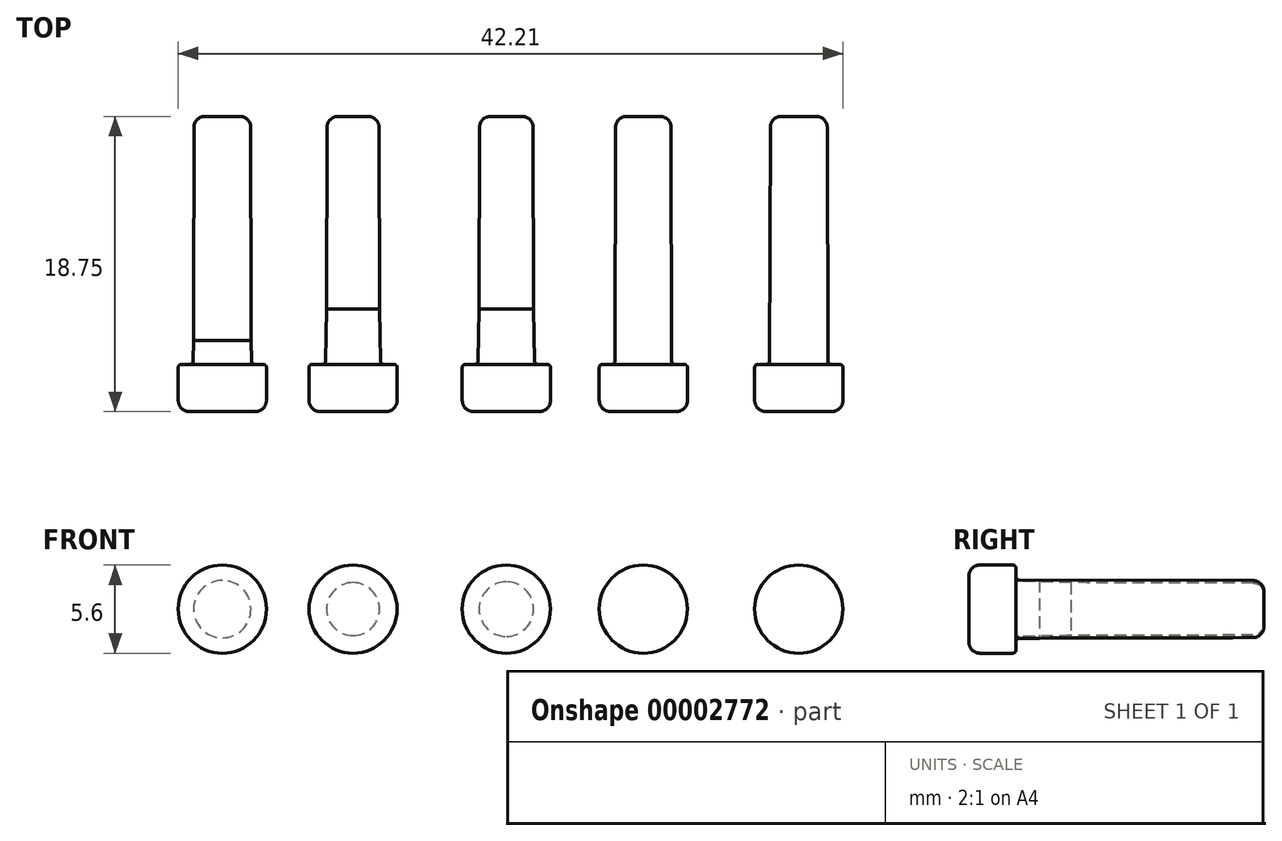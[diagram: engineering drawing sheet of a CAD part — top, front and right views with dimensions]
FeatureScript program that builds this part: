
annotation { "Feature Type Name" : "Feature", "Feature Type Description" : "" }
export const myFeature = defineFeature(function(context is Context, id is Id, definition is map)
    precondition{}
    {
        {
            var Q0;
            Q0=qCreatedBy(makeId("Top.planeOp"),FACE);
            var sketch = newSketch(context, id + "F0", { "sketchPlane" : qUnion([Q0])});
            skLineSegment(sketch, "E0", {"start": v(0, 0) * mm, "end": v(-2.8, 0) * mm});
            skLineSegment(sketch, "E1", {"start": v(-2.8, 0) * mm, "end": v(-2.8, 3) * mm});
            skLineSegment(sketch, "E2", {"start": v(-2.8, 3) * mm, "end": v(-1.8, 3) * mm});
            skLineSegment(sketch, "E3", {"start": v(-1.7, 18.75) * mm, "end": v(0, 18.75) * mm});
            skLineSegment(sketch, "E4", {"start": v(0, 18.75) * mm, "end": v(0, 0) * mm});
            skLineSegment(sketch, "E5", {"start": v(-9.74, 0) * mm, "end": v(-12.54, 0) * mm});
            skLineSegment(sketch, "E6", {"start": v(-12.54, 0) * mm, "end": v(-12.54, 3) * mm});
            skLineSegment(sketch, "E7", {"start": v(-12.54, 3) * mm, "end": v(-11.49, 3) * mm});
            skLineSegment(sketch, "E8", {"start": v(-11.39, 18.75) * mm, "end": v(-9.74, 18.75) * mm});
            skLineSegment(sketch, "E9", {"start": v(-9.74, 18.75) * mm, "end": v(-9.74, 0) * mm});
            skLineSegment(sketch, "E10", {"start": v(8.7, 0) * mm, "end": v(5.9, 0) * mm});
            skLineSegment(sketch, "E11", {"start": v(5.9, 0) * mm, "end": v(5.9, 3) * mm});
            skLineSegment(sketch, "E12", {"start": v(5.9, 3) * mm, "end": v(6.9, 3) * mm});
            skLineSegment(sketch, "E13", {"start": v(6.9, 3) * mm, "end": v(6.94, 18.75) * mm});
            skLineSegment(sketch, "E14", {"start": v(6.94, 18.75) * mm, "end": v(8.7, 18.75) * mm});
            skLineSegment(sketch, "E15", {"start": v(8.7, 18.75) * mm, "end": v(8.7, 0) * mm});
            skLineSegment(sketch, "E16", {"start": v(18.57, 0) * mm, "end": v(15.77, 0) * mm});
            skLineSegment(sketch, "E17", {"start": v(15.77, 0) * mm, "end": v(15.77, 3) * mm});
            skLineSegment(sketch, "E18", {"start": v(15.77, 3) * mm, "end": v(16.72, 3) * mm});
            skLineSegment(sketch, "E19", {"start": v(16.72, 3) * mm, "end": v(16.76, 18.75) * mm});
            skLineSegment(sketch, "E20", {"start": v(16.76, 18.75) * mm, "end": v(18.57, 18.75) * mm});
            skLineSegment(sketch, "E21", {"start": v(18.57, 18.75) * mm, "end": v(18.57, 0) * mm});
            skLineSegment(sketch, "E22", {"start": v(-18.04, 0) * mm, "end": v(-20.84, 0) * mm});
            skLineSegment(sketch, "E23", {"start": v(-20.84, 0) * mm, "end": v(-20.84, 3) * mm});
            skLineSegment(sketch, "E24", {"start": v(-20.84, 3) * mm, "end": v(-19.89, 3) * mm});
            skLineSegment(sketch, "E25", {"start": v(-19.84, 18.75) * mm, "end": v(-18.04, 18.75) * mm});
            skLineSegment(sketch, "E26", {"start": v(-18.04, 18.75) * mm, "end": v(-18.04, 0) * mm});
            skLineSegment(sketch, "E27", {"start": v(-1.8, 3) * mm, "end": v(-1.77, 4.5) * mm});
            skLineSegment(sketch, "E28", {"start": v(-1.77, 4.5) * mm, "end": v(-1.73, 6.5) * mm});
            skLineSegment(sketch, "E29", {"start": v(-1.73, 6.5) * mm, "end": v(-1.7, 18.75) * mm});
            skLineSegment(sketch, "E30", {"start": v(-11.49, 3) * mm, "end": v(-11.46, 4.5) * mm});
            skLineSegment(sketch, "E31", {"start": v(-11.46, 4.5) * mm, "end": v(-11.42, 6.5) * mm});
            skLineSegment(sketch, "E32", {"start": v(-11.42, 6.5) * mm, "end": v(-11.39, 18.75) * mm});
            skLineSegment(sketch, "E33", {"start": v(-19.89, 3) * mm, "end": v(-19.86, 4.5) * mm});
            skLineSegment(sketch, "E34", {"start": v(-19.86, 4.5) * mm, "end": v(-19.87, 6.5) * mm});
            skLineSegment(sketch, "E35", {"start": v(-19.87, 6.5) * mm, "end": v(-19.84, 18.75) * mm});
            skSolve(sketch);
        }
        {
            var Q0;
            Q0=makeQuery(id+"F0.imprint","IMPRINT",FACE,{"disambiguationData":[TD([[makeQuery(id+"F0.imprint","IMPRINT",EDGE,{"derivedFrom":sQuery(id+"F0.wireOp",EDGE,"E22")}),-1.0]])]});
            var Q1;
            Q1=sQuery(id+"F0.wireOp",EDGE,"E26");
            revolve(context, id + "F1", {"entities" : qUnion([Q0]), "axis" : qUnion([Q1]), "revolveType" : RevolveType.FULL});
        }
        {
            var Q0;
            Q0=makeQuery(id+"F0.imprint","IMPRINT",FACE,{"disambiguationData":[TD([[makeQuery(id+"F0.imprint","IMPRINT",EDGE,{"derivedFrom":sQuery(id+"F0.wireOp",EDGE,"E5")}),-1.0]])]});
            var Q1;
            Q1=sQuery(id+"F0.wireOp",EDGE,"E9");
            revolve(context, id + "F2", {"entities" : qUnion([Q0]), "axis" : qUnion([Q1]), "revolveType" : RevolveType.FULL});
        }
        {
            var Q0;
            Q0=makeQuery(id+"F0.imprint","IMPRINT",FACE,{"disambiguationData":[TD([[makeQuery(id+"F0.imprint","IMPRINT",EDGE,{"derivedFrom":sQuery(id+"F0.wireOp",EDGE,"E0")}),-1.0]])]});
            var Q1;
            Q1=sQuery(id+"F0.wireOp",EDGE,"E4");
            revolve(context, id + "F3", {"entities" : qUnion([Q0]), "axis" : qUnion([Q1]), "revolveType" : RevolveType.FULL});
        }
        {
            var Q0;
            Q0=makeQuery(id+"F0.imprint","IMPRINT",FACE,{"disambiguationData":[TD([[makeQuery(id+"F0.imprint","IMPRINT",EDGE,{"derivedFrom":sQuery(id+"F0.wireOp",EDGE,"E10")}),-1.0]])]});
            var Q1;
            Q1=sQuery(id+"F0.wireOp",EDGE,"E15");
            revolve(context, id + "F4", {"entities" : qUnion([Q0]), "axis" : qUnion([Q1]), "revolveType" : RevolveType.FULL});
        }
        {
            var Q0;
            Q0=makeQuery(id+"F0.imprint","IMPRINT",FACE,{"disambiguationData":[TD([[makeQuery(id+"F0.imprint","IMPRINT",EDGE,{"derivedFrom":sQuery(id+"F0.wireOp",EDGE,"E16")}),-1.0]])]});
            var Q1;
            Q1=sQuery(id+"F0.wireOp",EDGE,"E21");
            revolve(context, id + "F5", {"entities" : qUnion([Q0]), "axis" : qUnion([Q1]), "revolveType" : RevolveType.FULL});
        }
        {
            var Q0;
            Q0=makeQuery(id+"F1.opRevolve","SWEPT_EDGE",EDGE,{"disambiguationData":[OSD([sQuery(id+"F0.wireOp",EDGE,"E23"),sQuery(id+"F0.wireOp",EDGE,"E24")])]});
            var Q1;
            Q1=makeQuery(id+"F2.opRevolve","SWEPT_EDGE",EDGE,{"disambiguationData":[OSD([sQuery(id+"F0.wireOp",EDGE,"E6"),sQuery(id+"F0.wireOp",EDGE,"E7")])]});
            var Q2;
            Q2=makeQuery(id+"F3.opRevolve","SWEPT_EDGE",EDGE,{"disambiguationData":[OSD([sQuery(id+"F0.wireOp",EDGE,"E1"),sQuery(id+"F0.wireOp",EDGE,"E2")])]});
            var Q3;
            Q3=makeQuery(id+"F4.opRevolve","SWEPT_EDGE",EDGE,{"disambiguationData":[OSD([sQuery(id+"F0.wireOp",EDGE,"E11"),sQuery(id+"F0.wireOp",EDGE,"E12")])]});
            var Q4;
            Q4=makeQuery(id+"F5.opRevolve","SWEPT_EDGE",EDGE,{"disambiguationData":[OSD([sQuery(id+"F0.wireOp",EDGE,"E17"),sQuery(id+"F0.wireOp",EDGE,"E18")])]});
            var Q5;
            Q5=makeQuery(id+"F1.opRevolve","SWEPT_EDGE",EDGE,{"disambiguationData":[OSD([sQuery(id+"F0.wireOp",EDGE,"E24"),sQuery(id+"F0.wireOp",EDGE,"3260943c-5b43-4652-a50e-b8a2948cb4cb")])]});
            var Q6;
            Q6=makeQuery(id+"F2.opRevolve","SWEPT_EDGE",EDGE,{"disambiguationData":[OSD([sQuery(id+"F0.wireOp",EDGE,"E7"),sQuery(id+"F0.wireOp",EDGE,"40821458-fe53-42d1-9adc-950e0fd55064")])]});
            var Q7;
            Q7=makeQuery(id+"F3.opRevolve","SWEPT_EDGE",EDGE,{"disambiguationData":[OSD([sQuery(id+"F0.wireOp",EDGE,"E2"),sQuery(id+"F0.wireOp",EDGE,"8a6967c1-1885-4109-9060-1418cffab7ec")])]});
            var Q8;
            Q8=makeQuery(id+"F4.opRevolve","SWEPT_EDGE",EDGE,{"disambiguationData":[OSD([sQuery(id+"F0.wireOp",EDGE,"E12"),sQuery(id+"F0.wireOp",EDGE,"E13")])]});
            var Q9;
            Q9=makeQuery(id+"F5.opRevolve","SWEPT_EDGE",EDGE,{"disambiguationData":[OSD([sQuery(id+"F0.wireOp",EDGE,"E18"),sQuery(id+"F0.wireOp",EDGE,"E19")])]});
            fillet(context, id + "F6", {"entities" : qUnion([Q0, Q1, Q2, Q3, Q4, Q5, Q6, Q7, Q8, Q9]), "radius" : .2 * mm, "tangentPropagation" : true, "allowEdgeOverflow" : false});
        }
        {
            var Q0;
            Q0=makeQuery(id+"F1.opRevolve","SWEPT_EDGE",EDGE,{"disambiguationData":[OSD([sQuery(id+"F0.wireOp",EDGE,"3260943c-5b43-4652-a50e-b8a2948cb4cb"),sQuery(id+"F0.wireOp",EDGE,"E25")])]});
            var Q1;
            Q1=makeQuery(id+"F2.opRevolve","SWEPT_EDGE",EDGE,{"disambiguationData":[OSD([sQuery(id+"F0.wireOp",EDGE,"40821458-fe53-42d1-9adc-950e0fd55064"),sQuery(id+"F0.wireOp",EDGE,"E8")])]});
            var Q2;
            Q2=makeQuery(id+"F3.opRevolve","SWEPT_EDGE",EDGE,{"disambiguationData":[OSD([sQuery(id+"F0.wireOp",EDGE,"8a6967c1-1885-4109-9060-1418cffab7ec"),sQuery(id+"F0.wireOp",EDGE,"E3")])]});
            var Q3;
            Q3=makeQuery(id+"F4.opRevolve","SWEPT_EDGE",EDGE,{"disambiguationData":[OSD([sQuery(id+"F0.wireOp",EDGE,"E13"),sQuery(id+"F0.wireOp",EDGE,"E14")])]});
            var Q4;
            Q4=makeQuery(id+"F5.opRevolve","SWEPT_EDGE",EDGE,{"disambiguationData":[OSD([sQuery(id+"F0.wireOp",EDGE,"E19"),sQuery(id+"F0.wireOp",EDGE,"E20")])]});
            var Q5;
            Q5=makeQuery(id+"F1.opRevolve","SWEPT_EDGE",EDGE,{"disambiguationData":[OSD([sQuery(id+"F0.wireOp",EDGE,"E22"),sQuery(id+"F0.wireOp",EDGE,"E23")])]});
            var Q6;
            Q6=makeQuery(id+"F2.opRevolve","SWEPT_EDGE",EDGE,{"disambiguationData":[OSD([sQuery(id+"F0.wireOp",EDGE,"E5"),sQuery(id+"F0.wireOp",EDGE,"E6")])]});
            var Q7;
            Q7=makeQuery(id+"F3.opRevolve","SWEPT_EDGE",EDGE,{"disambiguationData":[OSD([sQuery(id+"F0.wireOp",EDGE,"E0"),sQuery(id+"F0.wireOp",EDGE,"E1")])]});
            var Q8;
            Q8=makeQuery(id+"F4.opRevolve","SWEPT_EDGE",EDGE,{"disambiguationData":[OSD([sQuery(id+"F0.wireOp",EDGE,"E10"),sQuery(id+"F0.wireOp",EDGE,"E11")])]});
            var Q9;
            Q9=makeQuery(id+"F5.opRevolve","SWEPT_EDGE",EDGE,{"disambiguationData":[OSD([sQuery(id+"F0.wireOp",EDGE,"E16"),sQuery(id+"F0.wireOp",EDGE,"E17")])]});
            fillet(context, id + "F7", {"entities" : qUnion([Q0, Q1, Q2, Q3, Q4, Q5, Q6, Q7, Q8, Q9]), "radius" : .7 * mm, "tangentPropagation" : true, "allowEdgeOverflow" : false});
        }
    });
